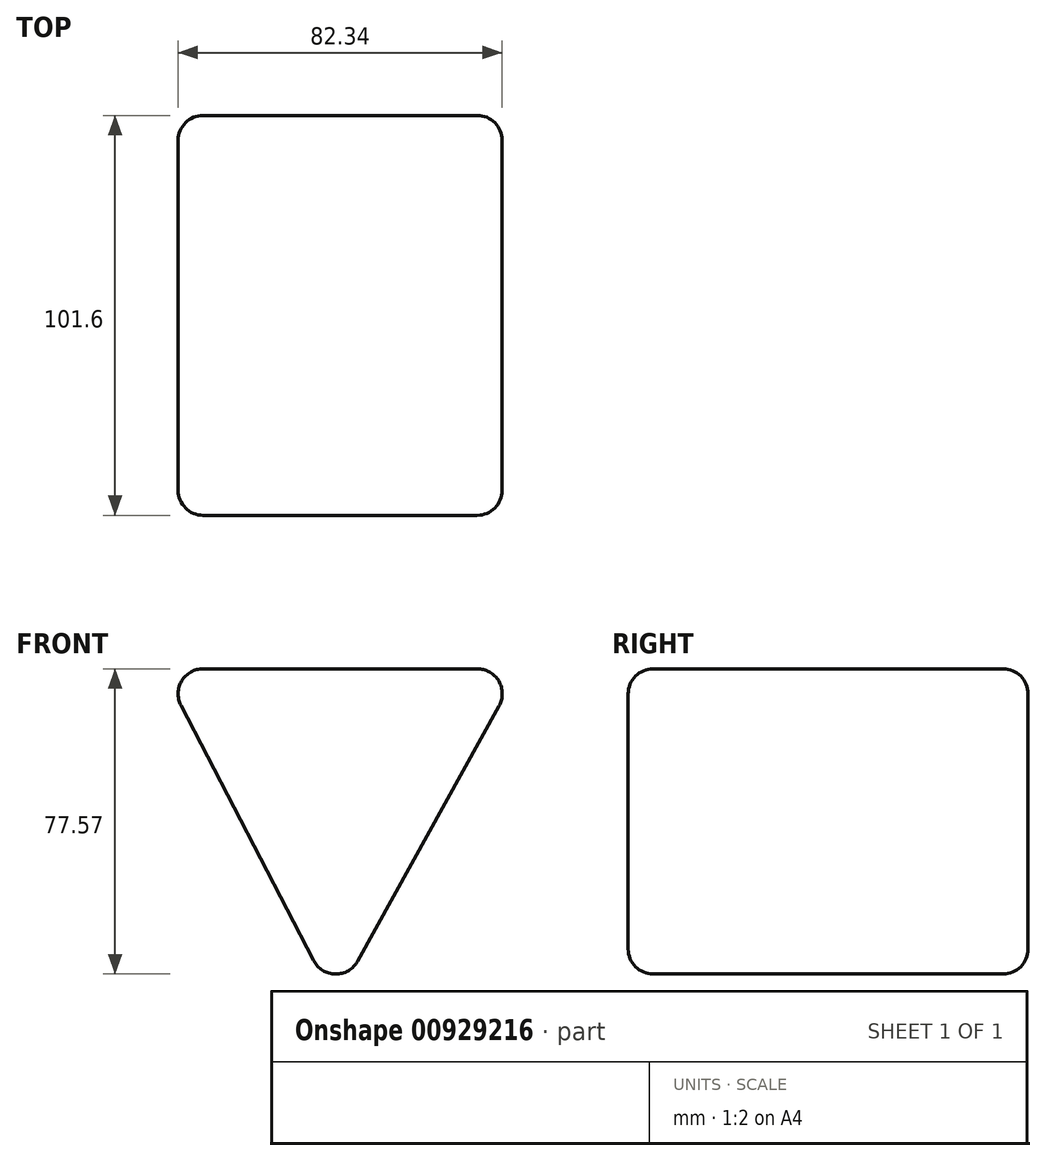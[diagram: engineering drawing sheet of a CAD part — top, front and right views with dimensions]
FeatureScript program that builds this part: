
annotation { "Feature Type Name" : "Feature", "Feature Type Description" : "" }
export const myFeature = defineFeature(function(context is Context, id is Id, definition is map)
    precondition{}
    {
        {
            var Q0;
            Q0=qCreatedBy(makeId("Front.planeOp"),FACE);
            var sketch = newSketch(context, id + "F0", { "sketchPlane" : qUnion([Q0])});
            skLineSegment(sketch, "E0", {"start": v(-43.98, 40.87) * mm, "end": v(46.89, 40.87) * mm});
            skLineSegment(sketch, "E1", {"start": v(46.89, 40.87) * mm, "end": v(0, -43.77) * mm});
            skLineSegment(sketch, "E2", {"start": v(0, -43.77) * mm, "end": v(-43.98, 40.87) * mm});
            skSolve(sketch);
        }
        {
            var Q0;
            Q0 = qSketchRegion(id + "F0", true);
            extrude(context, id + "F1", {"entities" : qUnion([Q0]), "endBound" : BoundingType.SYMMETRIC, "depth" : 101.6 * mm, "offsetDistance" : 25.4 * mm});
        }
        {
            var Q0;
            Q0=makeQuery(id+"F1.opExtrude","CAP_EDGE",EDGE,{"disambiguationData":[OSD([sQuery(id+"F0.wireOp",EDGE,"E0")])],"isStart":false});
            var Q1;
            Q1=makeQuery(id+"F1.opExtrude","CAP_EDGE",EDGE,{"disambiguationData":[OSD([sQuery(id+"F0.wireOp",EDGE,"E1")])],"isStart":false});
            var Q2;
            Q2=makeQuery(id+"F1.opExtrude","SWEPT_EDGE",EDGE,{"disambiguationData":[OSD([sQuery(id+"F0.wireOp",EDGE,"E1"),sQuery(id+"F0.wireOp",EDGE,"E2")])]});
            var Q3;
            Q3=makeQuery(id+"F1.opExtrude","CAP_EDGE",EDGE,{"disambiguationData":[OSD([sQuery(id+"F0.wireOp",EDGE,"E2")])],"isStart":true});
            var Q4;
            Q4=makeQuery(id+"F1.opExtrude","SWEPT_EDGE",EDGE,{"disambiguationData":[OSD([sQuery(id+"F0.wireOp",EDGE,"E0"),sQuery(id+"F0.wireOp",EDGE,"E2")])]});
            var Q5;
            Q5=makeQuery(id+"F1.opExtrude","SWEPT_EDGE",EDGE,{"disambiguationData":[OSD([sQuery(id+"F0.wireOp",EDGE,"E0"),sQuery(id+"F0.wireOp",EDGE,"E1")])]});
            var Q6;
            Q6=makeQuery(id+"F1.opExtrude","CAP_EDGE",EDGE,{"disambiguationData":[OSD([sQuery(id+"F0.wireOp",EDGE,"E1")])],"isStart":true});
            var Q7;
            Q7=makeQuery(id+"F1.opExtrude","CAP_EDGE",EDGE,{"disambiguationData":[OSD([sQuery(id+"F0.wireOp",EDGE,"E0")])],"isStart":true});
            var Q8;
            Q8=makeQuery(id+"F1.opExtrude","CAP_EDGE",EDGE,{"disambiguationData":[OSD([sQuery(id+"F0.wireOp",EDGE,"E2")])],"isStart":false});
            fillet(context, id + "F2", {"entities" : qUnion([Q0, Q1, Q2, Q3, Q4, Q5, Q6, Q7, Q8]), "radius" : 6.35 * mm, "tangentPropagation" : true, "allowEdgeOverflow" : false});
        }
    });
